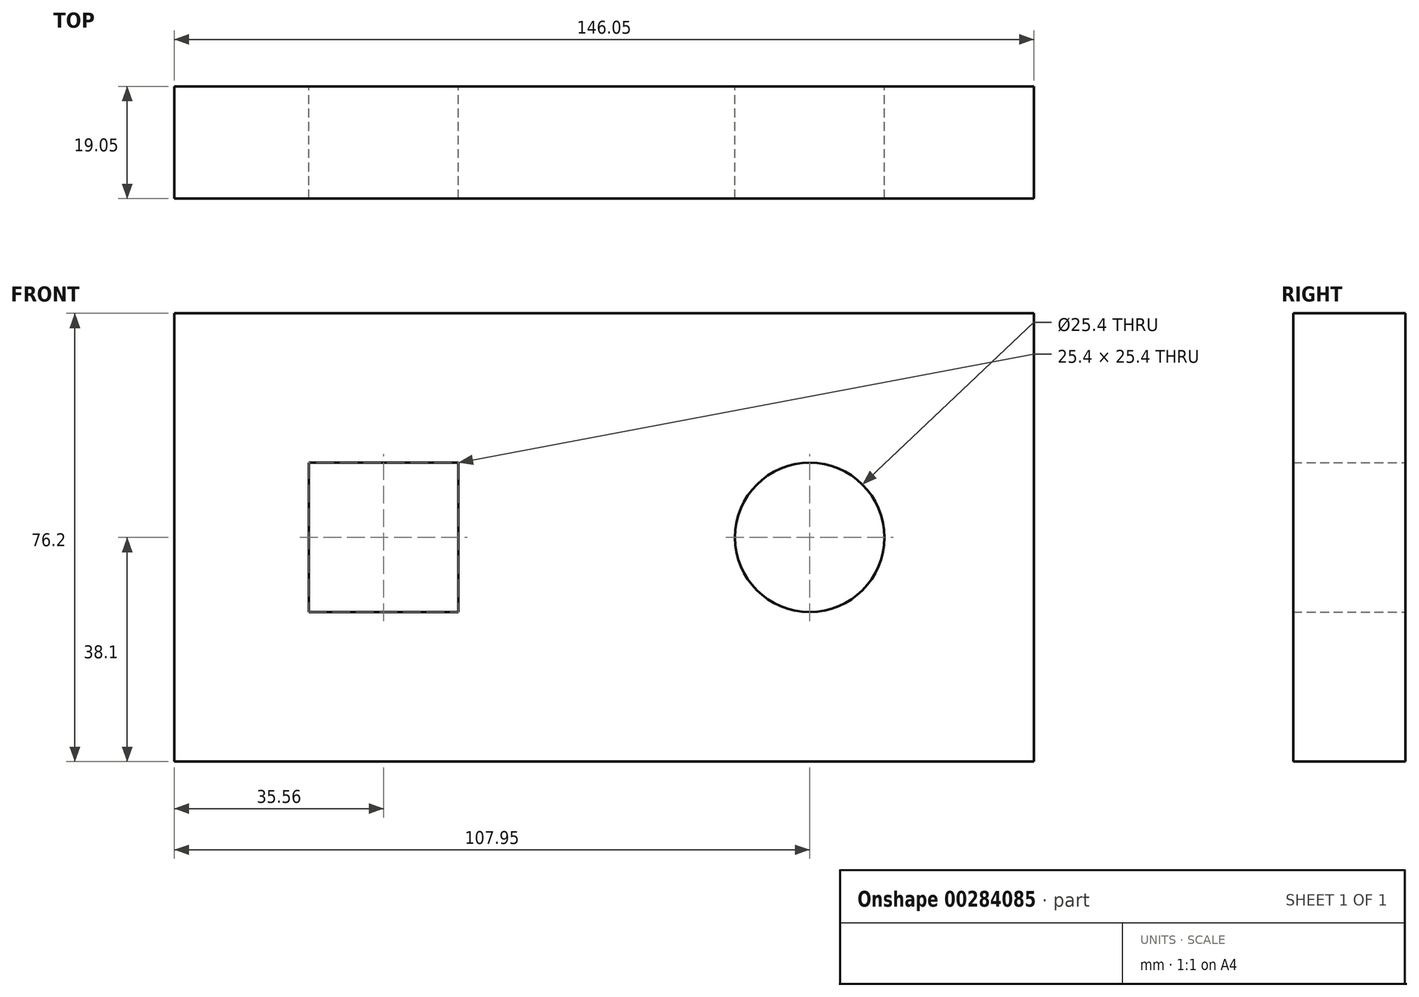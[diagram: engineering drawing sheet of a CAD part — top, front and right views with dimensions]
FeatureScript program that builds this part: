
annotation { "Feature Type Name" : "Feature", "Feature Type Description" : "" }
export const myFeature = defineFeature(function(context is Context, id is Id, definition is map)
    precondition{}
    {
        {
            var Q0;
            Q0=qCreatedBy(makeId("Front.planeOp"),FACE);
            var sketch = newSketch(context, id + "F0", { "sketchPlane" : qUnion([Q0])});
            skLineSegment(sketch, "E0.bottom", {"start": v(0, 0) * mm, "end": v(-146.05, 0) * mm});
            skLineSegment(sketch, "E0.top", {"start": v(0, 76.2) * mm, "end": v(-146.05, 76.2) * mm});
            skLineSegment(sketch, "E0.left", {"start": v(0, 0) * mm, "end": v(0, 76.2) * mm});
            skLineSegment(sketch, "E0.right", {"start": v(-146.05, 0) * mm, "end": v(-146.05, 76.2) * mm});
            skLineSegment(sketch, "E1.bottom", {"start": v(-97.8, 50.8) * mm, "end": v(-123.2, 50.8) * mm});
            skLineSegment(sketch, "E1.top", {"start": v(-97.8, 25.4) * mm, "end": v(-123.2, 25.4) * mm});
            skLineSegment(sketch, "E1.left", {"start": v(-97.8, 50.8) * mm, "end": v(-97.8, 25.4) * mm});
            skLineSegment(sketch, "E1.right", {"start": v(-123.2, 50.8) * mm, "end": v(-123.2, 25.4) * mm});
            skCircle(sketch, "E2", {"center": v(-38.1, 38.1) * mm, "radius": 12.7 * mm});
            skSolve(sketch);
        }
        {
            var Q0;
            Q0 = qSketchRegion(id + "F0", true);
            extrude(context, id + "F1", {"entities" : qUnion([Q0]), "depth" : 19.05 * mm});
        }
    });
